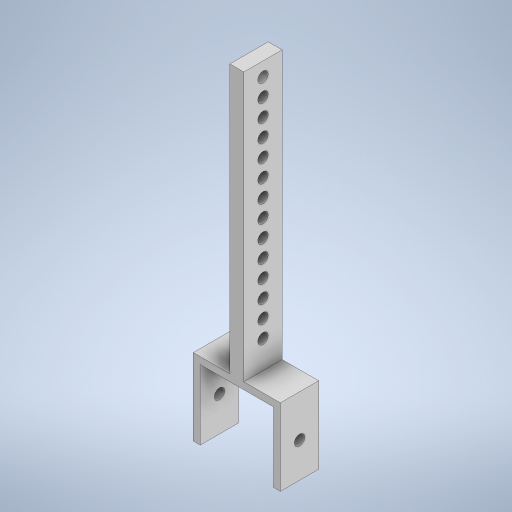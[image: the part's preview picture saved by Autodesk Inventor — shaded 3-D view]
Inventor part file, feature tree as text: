
AUTODESK INVENTOR PART (.ipt)
format: ipt  version: 2024 (Build 280153000, 153)  size: 313,856 bytes
history: native  units: mm
features: extrude x5, sketch x4, projected_geometry x2
ambient origin geometry x8: Origin, YZ Plane, XZ Plane, XY Plane, X Axis, Y Axis, Z Axis, Center Point
bodies: Body1 (feature_tree)
feature tree (11):
  extrude  "돌출3"  Depth=11.0mm
  sketch  "스케치5"
  extrude  "돌출4"  Depth=4.0mm
  extrude  "돌출5"  Depth=77.0mm TaperAngle=0.0deg
  extrude  "돌출6"  Depth=21.0mm
  extrude  "돌출7"  Depth=11.0mm
  sketch  "스케치4"
  sketch  "스케치6"
  projected_geometry  "투영된 루프1"
  sketch  "스케치7"
  projected_geometry  "투영된 루프2"
